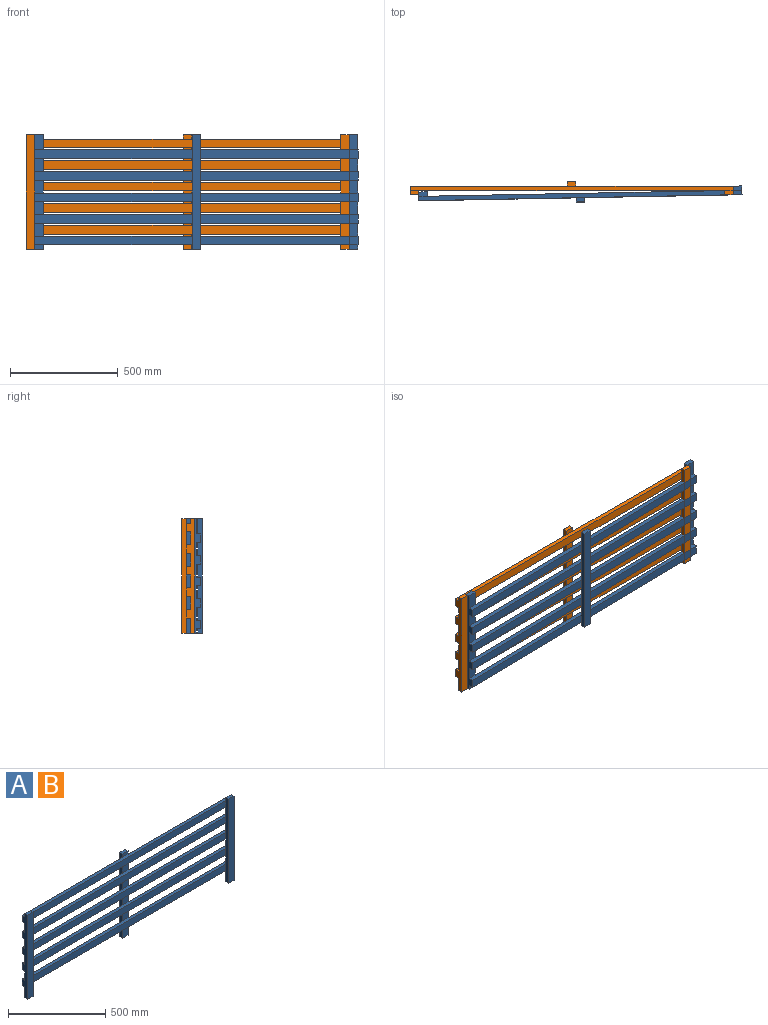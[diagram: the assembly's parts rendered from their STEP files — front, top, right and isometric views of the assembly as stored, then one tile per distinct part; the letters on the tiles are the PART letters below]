
ASSEMBLY  parts=2 mates=1
PART A: 58 faces, bbox 1500x60x530 mm
  f0: plane 730x40mm, normal (0,1,0), area 29200mm2, adj f2,f4,f6,f52
  f1: plane 1420x40mm, normal (0,-1,0), area 56800mm2, adj f2,f4,f42,f47
  f2: plane 1500x20mm, normal (0,0,-1), area 30000mm2, adj f0,f1,f3,f5,f6,f7,f8,f9
  f3: plane 730x40mm, normal (0,1,0), area 29200mm2, adj f2,f4,f5,f54
  f4: plane 1500x20mm, normal (0,0,1), area 30000mm2, adj f0,f1,f3,f5,f6,f15,f16,f17
  f5: plane 530x40mm, normal (1,0,0), area 14600mm2, adj f2,f3,f4,f9,f12,f13,f14,f17
  f6: plane 530x40mm, normal (-1,0,0), area 14600mm2, adj f0,f2,f4,f8,f10,f12,f14,f16
  f7: plane 70x40mm, normal (0,-1,0), area 2800mm2, adj f2,f52,f54,f56
  f8: plane 70x40mm, normal (0,1,0), area 2800mm2, adj f2,f6,f42,f43
  f9: plane 70x40mm, normal (0,1,0), area 2800mm2, adj f2,f5,f47,f49
  f10: plane 730x40mm, normal (0,1,0), area 29200mm2, adj f6,f12,f14,f52
  f11: plane 1420x40mm, normal (0,-1,0), area 56800mm2, adj f12,f14,f42,f47
  f12: plane 1500x20mm, normal (0,0,-1), area 30000mm2, adj f5,f6,f10,f11,f13,f15,f16,f17
  f13: plane 730x40mm, normal (0,1,0), area 29200mm2, adj f5,f12,f14,f54
  f14: plane 1500x20mm, normal (0,0,1), area 30000mm2, adj f5,f6,f10,f11,f13,f23,f24,f25
  f15: plane 60x40mm, normal (0,-1,0), area 2400mm2, adj f4,f12,f52,f54
  f16: plane 60x40mm, normal (0,1,0), area 2400mm2, adj f4,f6,f12,f42
  f17: plane 60x40mm, normal (0,1,0), area 2400mm2, adj f4,f5,f12,f47
  f18: plane 730x40mm, normal (0,1,0), area 29200mm2, adj f6,f20,f22,f52
  f19: plane 1420x40mm, normal (0,-1,0), area 56800mm2, adj f20,f22,f42,f47
  f20: plane 1500x20mm, normal (0,0,-1), area 30000mm2, adj f5,f6,f18,f19,f21,f23,f24,f25
  f21: plane 730x40mm, normal (0,1,0), area 29200mm2, adj f5,f20,f22,f54
  f22: plane 1500x20mm, normal (0,0,1), area 30000mm2, adj f5,f6,f18,f19,f21,f31,f32,f33
  f23: plane 60x40mm, normal (0,-1,0), area 2400mm2, adj f14,f20,f52,f54
  f24: plane 60x40mm, normal (0,1,0), area 2400mm2, adj f6,f14,f20,f42
  f25: plane 60x40mm, normal (0,1,0), area 2400mm2, adj f5,f14,f20,f47
  f26: plane 730x40mm, normal (0,1,0), area 29200mm2, adj f6,f28,f30,f52
  f27: plane 1420x40mm, normal (0,-1,0), area 56800mm2, adj f28,f30,f42,f47
  f28: plane 1500x20mm, normal (0,0,-1), area 30000mm2, adj f5,f6,f26,f27,f29,f31,f32,f33
  f29: plane 730x40mm, normal (0,1,0), area 29200mm2, adj f5,f28,f30,f54
  f30: plane 1500x20mm, normal (0,0,1), area 30000mm2, adj f5,f6,f26,f27,f29,f39,f45,f51
  f31: plane 60x40mm, normal (0,-1,0), area 2400mm2, adj f22,f28,f52,f54
  f32: plane 60x40mm, normal (0,1,0), area 2400mm2, adj f6,f22,f28,f42
  f33: plane 60x40mm, normal (0,1,0), area 2400mm2, adj f5,f22,f28,f47
  f34: plane 730x40mm, normal (0,1,0), area 29200mm2, adj f6,f36,f38,f52
  f35: plane 1420x40mm, normal (0,-1,0), area 56800mm2, adj f36,f38,f42,f47
  f36: plane 1500x20mm, normal (0,0,-1), area 30000mm2, adj f5,f6,f34,f35,f37,f39,f45,f51
  f37: plane 730x40mm, normal (0,1,0), area 29200mm2, adj f5,f36,f38,f54
  f38: plane 1500x20mm, normal (0,0,1), area 30000mm2, adj f5,f6,f34,f35,f37,f40,f46,f53
  f39: plane 60x40mm, normal (0,1,0), area 2400mm2, adj f6,f30,f36,f42
  f40: plane 40x20mm, normal (0,1,0), area 800mm2, adj f6,f38,f42,f44
  f41: plane 530x40mm, normal (0,-1,0), area 21200mm2, adj f6,f42,f43,f44
  f42: plane 530x20mm, normal (1,0,0), area 10600mm2, adj f1,f8,f11,f16,f19,f24,f27,f32
  f43: plane 40x20mm, normal (0,0,-1), area 800mm2, adj f6,f8,f41,f42
  f44: plane 40x20mm, normal (0,0,1), area 800mm2, adj f6,f40,f41,f42
  f45: plane 60x40mm, normal (0,1,0), area 2400mm2, adj f5,f30,f36,f47
  f46: plane 40x20mm, normal (0,1,0), area 800mm2, adj f5,f38,f47,f50
  f47: plane 530x20mm, normal (-1,0,0), area 10600mm2, adj f1,f9,f11,f17,f19,f25,f27,f33
  f48: plane 530x40mm, normal (0,-1,0), area 21200mm2, adj f5,f47,f49,f50
  f49: plane 40x20mm, normal (0,0,-1), area 800mm2, adj f5,f9,f47,f48
  f50: plane 40x20mm, normal (0,0,1), area 800mm2, adj f5,f46,f47,f48
  f51: plane 60x40mm, normal (0,-1,0), area 2400mm2, adj f30,f36,f52,f54
  f52: plane 530x20mm, normal (-1,0,0), area 10600mm2, adj f0,f7,f10,f15,f18,f23,f26,f31
  f53: plane 40x20mm, normal (0,-1,0), area 800mm2, adj f38,f52,f54,f57
  f54: plane 530x20mm, normal (1,0,0), area 10600mm2, adj f3,f7,f13,f15,f21,f23,f29,f31
  f55: plane 530x40mm, normal (0,1,0), area 21200mm2, adj f52,f54,f56,f57
  f56: plane 40x20mm, normal (0,0,-1), area 800mm2, adj f7,f52,f54,f55
  f57: plane 40x20mm, normal (0,0,1), area 800mm2, adj f52,f53,f54,f55
PART B: same geometry as A
PLACE A rot(axis=(1,0.01,0),180deg) t=(40.66,-53.41,440)mm
PLACE B t=(0,-20,90)mm
MATE planar B.f56 <-> A.f50  axis (0,0,-1) through (0,0,0)mm
